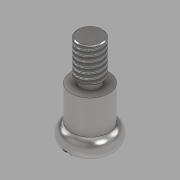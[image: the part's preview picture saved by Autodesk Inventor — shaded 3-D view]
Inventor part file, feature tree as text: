
AUTODESK INVENTOR PART (.ipt)
format: ipt  version: 2020 (Build 240168000, 168)  size: 147,968 bytes
history: native  units: in
note: dims shown in document units (in); Inventor stores cm internally (conversion verified against a paired STEP export)
features: sketch x2, other x1, revolve x1, thread x1, extrude x1
ambient origin geometry x8: Origin, YZ Plane, XZ Plane, XY Plane, X Axis, Y Axis, Z Axis, Center Point
bodies: Body1 (feature_tree)
feature tree (6):
  other  "Sólido1"
  revolve  "Revolución1"  [1 undecoded]
  thread  "Rosca1"  [1 undecoded]
  extrude  "Extrusión1"  Depth=0.0312in
  sketch  "Boceto1"  dims[d0=0.0625in d1=0.4688in d2=0.005in]
  sketch  "Boceto2"  dims[d3=0.005in d4=0.172in d5=0.0312in d6=0.0156in d7=0.172in d8=0.005in d9=0.005in d10=0.0938in d11=0.2656in d12=0.1in d13=0.05in d14=0.075in d15=90.0deg d16=0.162in d17=0.0in d18=0.0312in d19=0.0156in d20=0.0312in d21=0.0in]
note: 2 required parameter values undecoded (feature->parameter linkage not recoverable at this tier; creation-order binding heuristic only, values carry confidence <= 0.55)